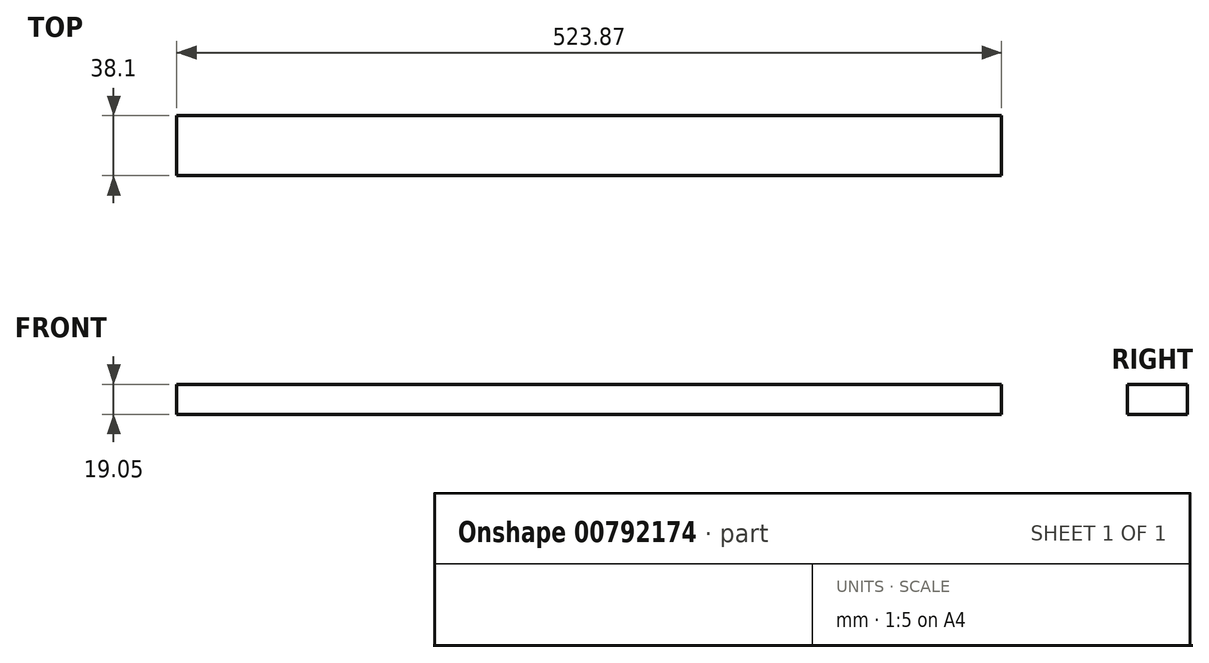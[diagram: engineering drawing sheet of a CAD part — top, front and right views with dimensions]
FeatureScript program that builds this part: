
annotation { "Feature Type Name" : "Feature", "Feature Type Description" : "" }
export const myFeature = defineFeature(function(context is Context, id is Id, definition is map)
    precondition{}
    {
        {
            var Q0;
            Q0=qCreatedBy(makeId("Top.planeOp"),FACE);
            var sketch = newSketch(context, id + "F0", { "sketchPlane" : qUnion([Q0])});
            skLineSegment(sketch, "E0.bottom", {"start": v(465.83, 0) * mm, "end": v(-58.04, 0) * mm});
            skLineSegment(sketch, "E0.top", {"start": v(465.83, 38.1) * mm, "end": v(-58.04, 38.1) * mm});
            skLineSegment(sketch, "E0.left", {"start": v(465.83, 0) * mm, "end": v(465.83, 38.1) * mm});
            skLineSegment(sketch, "E0.right", {"start": v(-58.04, 0) * mm, "end": v(-58.04, 38.1) * mm});
            skSolve(sketch);
        }
        {
            var Q0;
            Q0 = qSketchRegion(id + "F0", true);
            extrude(context, id + "F1", {"entities" : qUnion([Q0]), "depth" : 19.05 * mm, "offsetDistance" : 25.4 * mm});
        }
    });
